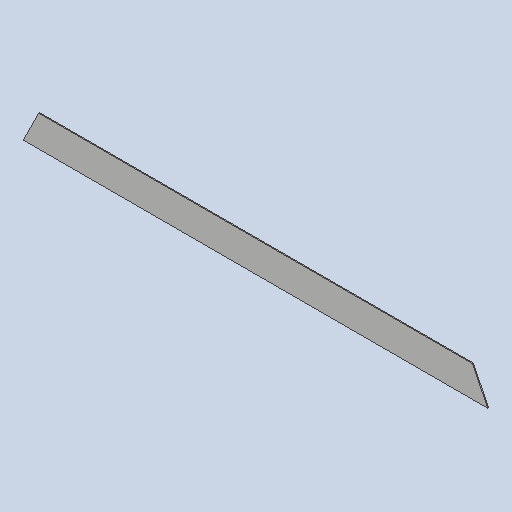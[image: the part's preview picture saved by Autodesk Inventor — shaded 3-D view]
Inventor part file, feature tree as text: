
AUTODESK INVENTOR PART (.ipt)
format: ipt  version: 2025 (Build 290162010, 162A)  size: 276,480 bytes
history: native  units: mm
features: other x3, sheet_metal_op x1, sketch x1
ambient origin geometry x8: Origin, YZ Plane, XZ Plane, XY Plane, X Axis, Y Axis, Z Axis, Center Point
bodies: Solid1 (feature_tree)
feature tree (5):
  other  "MSC 204 GRID"
  sheet_metal_op  "Face1"
  sketch  "Sketch1"  dims[d0=100.0mm d1=1800.0mm d2=3.0mm d3=20.333086mm d6=698.5mm d7=20.333086mm d8=698.5mm]
  other  "Plate1"
  other  "Definition1"
